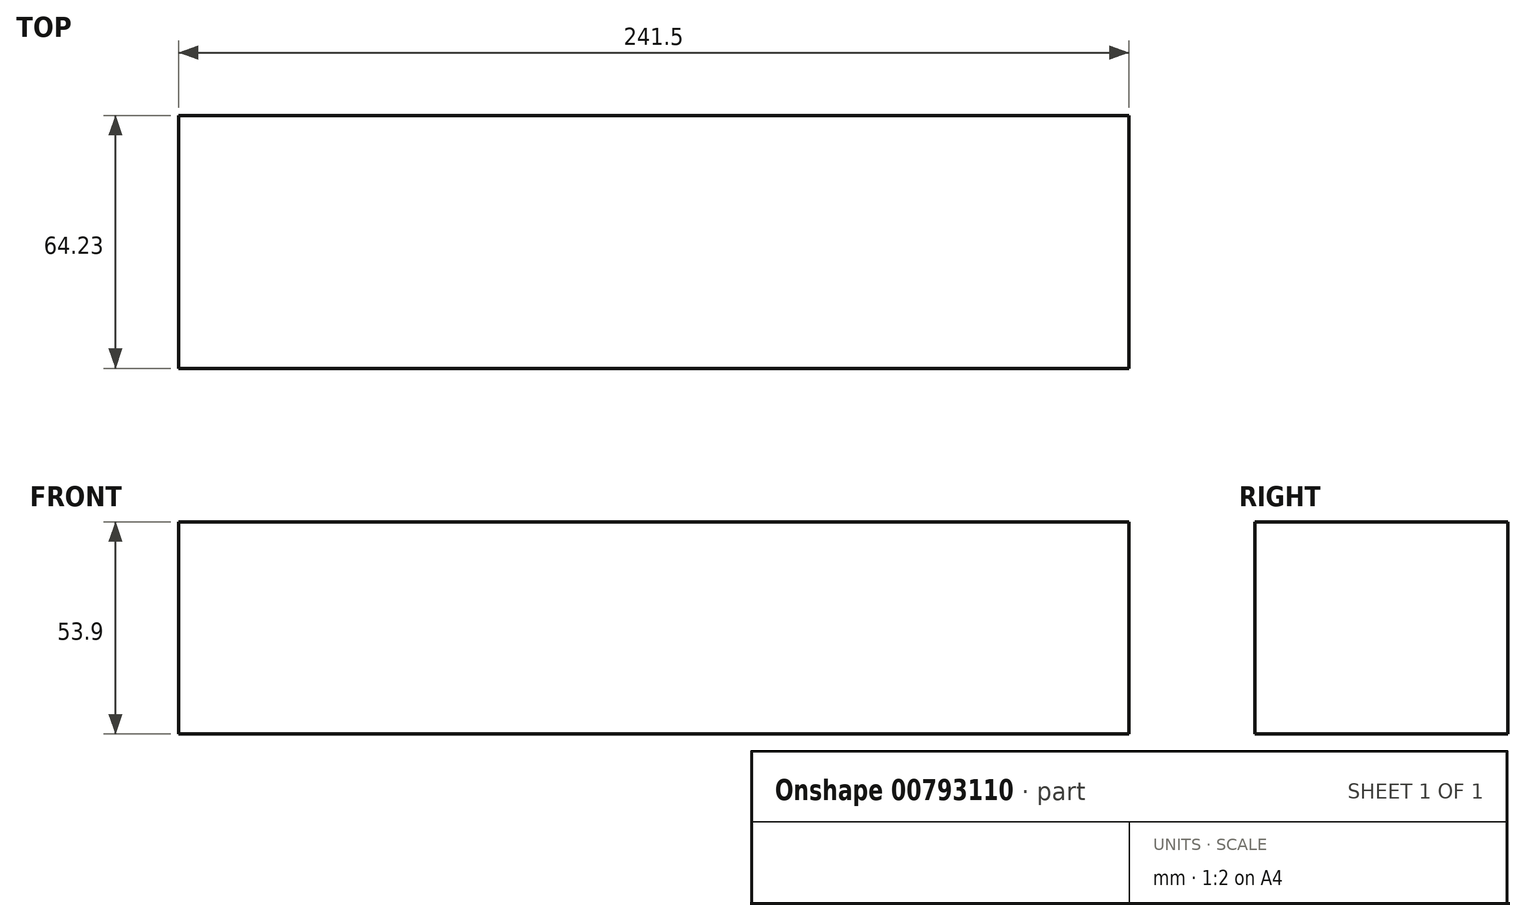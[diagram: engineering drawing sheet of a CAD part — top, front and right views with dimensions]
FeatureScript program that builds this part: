
annotation { "Feature Type Name" : "Feature", "Feature Type Description" : "" }
export const myFeature = defineFeature(function(context is Context, id is Id, definition is map)
    precondition{}
    {
        {
            var Q0;
            Q0=qCreatedBy(makeId("Right.planeOp"),FACE);
            var sketch = newSketch(context, id + "F0", { "sketchPlane" : qUnion([Q0])});
            skLineSegment(sketch, "E0.bottom", {"start": v(-35.1, 53.9) * mm, "end": v(29.14, 53.9) * mm});
            skLineSegment(sketch, "E0.top", {"start": v(-35.1, 0) * mm, "end": v(29.14, 0) * mm});
            skLineSegment(sketch, "E0.left", {"start": v(-35.1, 53.9) * mm, "end": v(-35.1, 0) * mm});
            skLineSegment(sketch, "E0.right", {"start": v(29.14, 53.9) * mm, "end": v(29.14, 0) * mm});
            skSolve(sketch);
        }
        {
            var Q0;
            Q0 = qSketchRegion(id + "F0", true);
            extrude(context, id + "F1", {"entities" : qUnion([Q0]), "depth" : 241.5 * mm, "offsetDistance" : 25 * mm});
        }
    });
